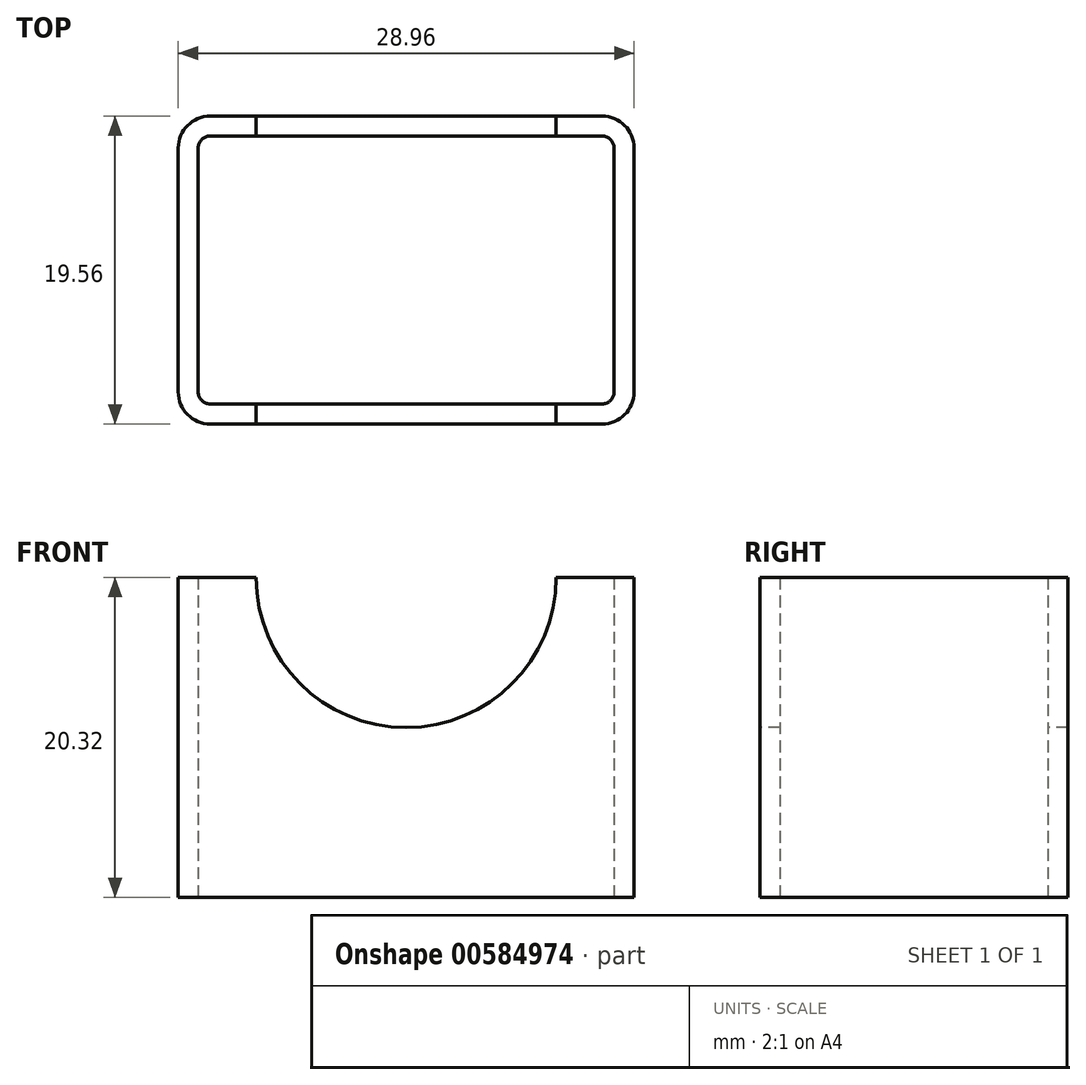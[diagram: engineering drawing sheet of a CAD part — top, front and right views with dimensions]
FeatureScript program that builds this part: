
annotation { "Feature Type Name" : "Feature", "Feature Type Description" : "" }
export const myFeature = defineFeature(function(context is Context, id is Id, definition is map)
    precondition{}
    {
        {
            var Q0;
            Q0=qCreatedBy(makeId("Top.planeOp"),FACE);
            var sketch = newSketch(context, id + "F0", { "sketchPlane" : qUnion([Q0])});
            skLineSegment(sketch, "E0.bottom", {"start": v(12.45, 8.5) * mm, "end": v(-12.45, 8.5) * mm});
            skLineSegment(sketch, "E0.top", {"start": v(12.45, -8.5) * mm, "end": v(-12.45, -8.5) * mm});
            skLineSegment(sketch, "E0.left", {"start": v(13.2, 7.75) * mm, "end": v(13.2, -7.75) * mm});
            skLineSegment(sketch, "E0.right", {"start": v(-13.2, 7.75) * mm, "end": v(-13.2, -7.75) * mm});
            skPoint(sketch, "E0.middle", {"position": v(0, 0) * mm});
            skLineSegment(sketch, "E1.bottom", {"start": v(12.45, 9.78) * mm, "end": v(-12.45, 9.78) * mm});
            skLineSegment(sketch, "E1.top", {"start": v(12.45, -9.78) * mm, "end": v(-12.45, -9.78) * mm});
            skLineSegment(sketch, "E1.left", {"start": v(14.48, 7.75) * mm, "end": v(14.48, -7.75) * mm});
            skLineSegment(sketch, "E1.right", {"start": v(-14.48, 7.75) * mm, "end": v(-14.48, -7.75) * mm});
            skPoint(sketch, "E2.visualSharp", {"position": v(-13.2, 8.5) * mm});
            skArc(sketch, "E2.filletArc", {"start": v(-12.45, 8.5) * mm, "mid": v(-12.98, 8.29) * mm, "end": v(-13.2, 7.75) * mm});
            skPoint(sketch, "E3.visualSharp", {"position": v(-13.2, -8.5) * mm});
            skArc(sketch, "E3.filletArc", {"start": v(-13.2, -7.75) * mm, "mid": v(-12.98, -8.29) * mm, "end": v(-12.45, -8.5) * mm});
            skPoint(sketch, "E4.visualSharp", {"position": v(13.2, -8.5) * mm});
            skArc(sketch, "E4.filletArc", {"start": v(12.45, -8.5) * mm, "mid": v(12.98, -8.29) * mm, "end": v(13.2, -7.75) * mm});
            skPoint(sketch, "E5.visualSharp", {"position": v(13.2, 8.5) * mm});
            skArc(sketch, "E5.filletArc", {"start": v(13.2, 7.75) * mm, "mid": v(12.98, 8.29) * mm, "end": v(12.45, 8.5) * mm});
            skPoint(sketch, "E6.visualSharp", {"position": v(-14.48, -9.78) * mm});
            skArc(sketch, "E6.filletArc", {"start": v(-14.48, -7.75) * mm, "mid": v(-13.88, -9.18) * mm, "end": v(-12.45, -9.78) * mm});
            skPoint(sketch, "E7.visualSharp", {"position": v(14.48, -9.78) * mm});
            skArc(sketch, "E7.filletArc", {"start": v(12.45, -9.78) * mm, "mid": v(13.88, -9.18) * mm, "end": v(14.48, -7.75) * mm});
            skPoint(sketch, "E8.visualSharp", {"position": v(-14.48, 9.78) * mm});
            skArc(sketch, "E8.filletArc", {"start": v(-12.45, 9.78) * mm, "mid": v(-13.88, 9.18) * mm, "end": v(-14.48, 7.75) * mm});
            skPoint(sketch, "E9.visualSharp", {"position": v(14.48, 9.78) * mm});
            skArc(sketch, "E9.filletArc", {"start": v(14.48, 7.75) * mm, "mid": v(13.88, 9.18) * mm, "end": v(12.45, 9.78) * mm});
            skSolve(sketch);
        }
        {
            var Q0;
            Q0 = qSketchRegion(id + "F0", true);
            extrude(context, id + "F1", {"entities" : qUnion([Q0]), "depth" : 20.32 * mm, "offsetDistance" : 25.4 * mm});
        }
        {
            var Q0;
            Q0=makeQuery(id+"F1.opExtrude","SWEPT_FACE",FACE,{"disambiguationData":[OSD([sQuery(id+"F0.wireOp",EDGE,"E1.top")])]});
            var sketch = newSketch(context, id + "F2", { "sketchPlane" : qUnion([Q0])});
            skCircle(sketch, "E10", {"center": v(0, 20.32) * mm, "radius": 9.53 * mm});
            skSolve(sketch);
        }
        {
            var Q0;
            Q0 = qSketchRegion(id + "F2", true);
            extrude(context, id + "F3", {"entities" : qUnion([Q0]), "operationType" : NewBodyOperationType.REMOVE, "endBound" : BoundingType.THROUGH_ALL, "oppositeDirection" : true, "depth" : 25.4 * mm, "offsetDistance" : 25.4 * mm});
        }
    });
